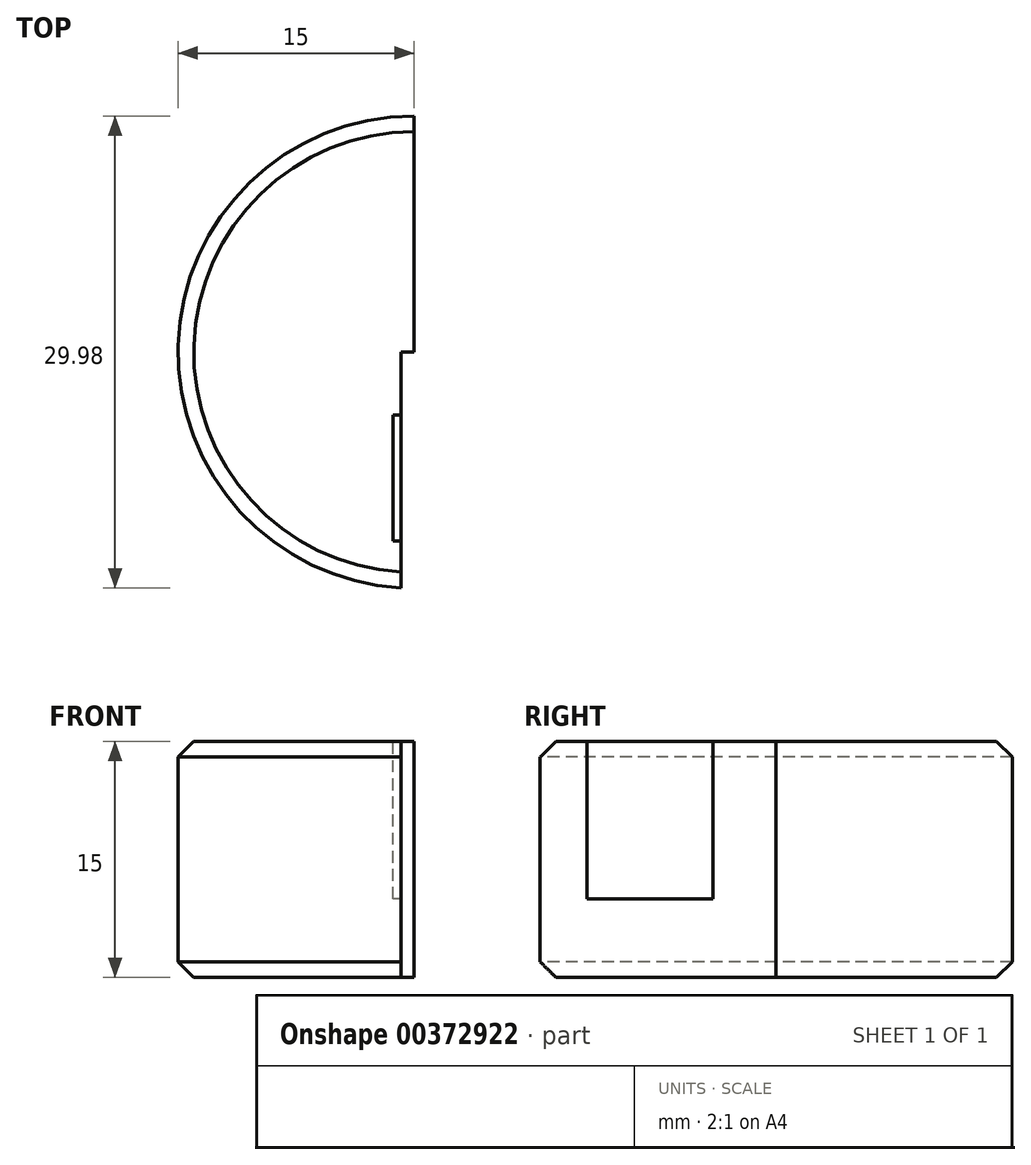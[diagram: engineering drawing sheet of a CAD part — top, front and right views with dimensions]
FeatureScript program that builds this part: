
annotation { "Feature Type Name" : "Feature", "Feature Type Description" : "" }
export const myFeature = defineFeature(function(context is Context, id is Id, definition is map)
    precondition{}
    {
        {
            var Q0;
            Q0=qCreatedBy(makeId("Top.planeOp"),FACE);
            var sketch = newSketch(context, id + "F0", { "sketchPlane" : qUnion([Q0])});
            skArc(sketch, "E0", {"start": v(0, 15) * mm, "mid": v(-15, 0) * mm, "end": v(0, -15) * mm});
            skLineSegment(sketch, "E1", {"start": v(0, 19.14) * mm, "end": v(0, -23.7) * mm, "construction": true});
            skLineSegment(sketch, "E2.bottom", {"start": v(0, -4) * mm, "end": v(-0.6, -4) * mm});
            skLineSegment(sketch, "E2.top", {"start": v(0, -12) * mm, "end": v(-0.6, -12) * mm});
            skLineSegment(sketch, "E2.left", {"start": v(0, -4) * mm, "end": v(0, -12) * mm});
            skLineSegment(sketch, "E2.right", {"start": v(-0.6, -4) * mm, "end": v(-0.6, -12) * mm});
            skLineSegment(sketch, "E3", {"start": v(0, 15) * mm, "end": v(0, -15) * mm});
            skSolve(sketch);
        }
        {
            var Q0;
            Q0 = qSketchRegion(id + "F0", true);
            extrude(context, id + "F1", {"entities" : qUnion([Q0]), "depth" : 15 * mm});
        }
        {
            var Q0;
            Q0=makeQuery(id+"F1.opExtrude","CAP_EDGE",EDGE,{"disambiguationData":[OSD([sQuery(id+"F0.wireOp",EDGE,"E0")])],"isStart":false});
            var Q1;
            Q1=makeQuery(id+"F1.opExtrude","CAP_EDGE",EDGE,{"disambiguationData":[OSD([sQuery(id+"F0.wireOp",EDGE,"E0")])],"isStart":true});
            chamfer(context, id + "F2", {"entities" : qUnion([Q0, Q1]), "width" : 1 * mm, "tangentPropagation" : true});
        }
        {
            var Q0;
            Q0=makeQuery(id+"F1.opExtrude","CAP_FACE",FACE,{"disambiguationData":[OSD([sQuery(id+"F0.wireOp",EDGE,"E0"),sQuery(id+"F0.wireOp",EDGE,"E3")])],"isStart":false});
            var sketch = newSketch(context, id + "F3", { "sketchPlane" : qUnion([Q0])});
            skLineSegment(sketch, "E4", {"start": v(0, 19.04) * mm, "end": v(0, 14.9) * mm, "construction": true});
            skLineSegment(sketch, "E5.bottom", {"start": v(0, 0) * mm, "end": v(-0.85, 0) * mm});
            skLineSegment(sketch, "E5.top", {"start": v(0, -15.63) * mm, "end": v(-0.85, -15.63) * mm});
            skLineSegment(sketch, "E5.left", {"start": v(0, 0) * mm, "end": v(0, -15.63) * mm});
            skLineSegment(sketch, "E5.right", {"start": v(-0.85, 0) * mm, "end": v(-0.85, -15.63) * mm});
            skLineSegment(sketch, "E6.trimOffspring", {"start": v(0, 0) * mm, "end": v(0, -15.63) * mm, "construction": true});
            skPoint(sketch, "E7.orphan", {"position": v(0, 4) * mm});
            skLineSegment(sketch, "E8.trimOffspring", {"start": v(0, -15.1) * mm, "end": v(0, -23.8) * mm, "construction": true});
            skSolve(sketch);
        }
        {
            var Q0;
            Q0 = qSketchRegion(id + "F3", true);
            extrude(context, id + "F4", {"entities" : qUnion([Q0]), "operationType" : NewBodyOperationType.REMOVE, "oppositeDirection" : true, "depth" : 25 * mm});
        }
        {
            var Q0;
            Q0=makeQuery(id+"F1.opExtrude","CAP_FACE",FACE,{"disambiguationData":[OSD([sQuery(id+"F0.wireOp",EDGE,"E0"),sQuery(id+"F0.wireOp",EDGE,"E3")])],"isStart":false});
            var sketch = newSketch(context, id + "F5", { "sketchPlane" : qUnion([Q0])});
            skLineSegment(sketch, "E9.bottom", {"start": v(-0.85, -12) * mm, "end": v(-1.35, -12) * mm});
            skLineSegment(sketch, "E9.top", {"start": v(-0.85, -4) * mm, "end": v(-1.35, -4) * mm});
            skLineSegment(sketch, "E9.left", {"start": v(-0.85, -12) * mm, "end": v(-0.85, -4) * mm});
            skLineSegment(sketch, "E9.right", {"start": v(-1.35, -12) * mm, "end": v(-1.35, -4) * mm});
            skSolve(sketch);
        }
        {
            var Q0;
            Q0=makeQuery(id+"F5.imprint","IMPRINT",FACE,{"disambiguationData":[TD([[makeQuery(id+"F5.imprint","IMPRINT",EDGE,{"derivedFrom":sQuery(id+"F5.wireOp",EDGE,"E9.bottom")}),-1.0]])]});
            extrude(context, id + "F6", {"entities" : qUnion([Q0]), "operationType" : NewBodyOperationType.REMOVE, "oppositeDirection" : true, "depth" : 10 * mm});
        }
    });
